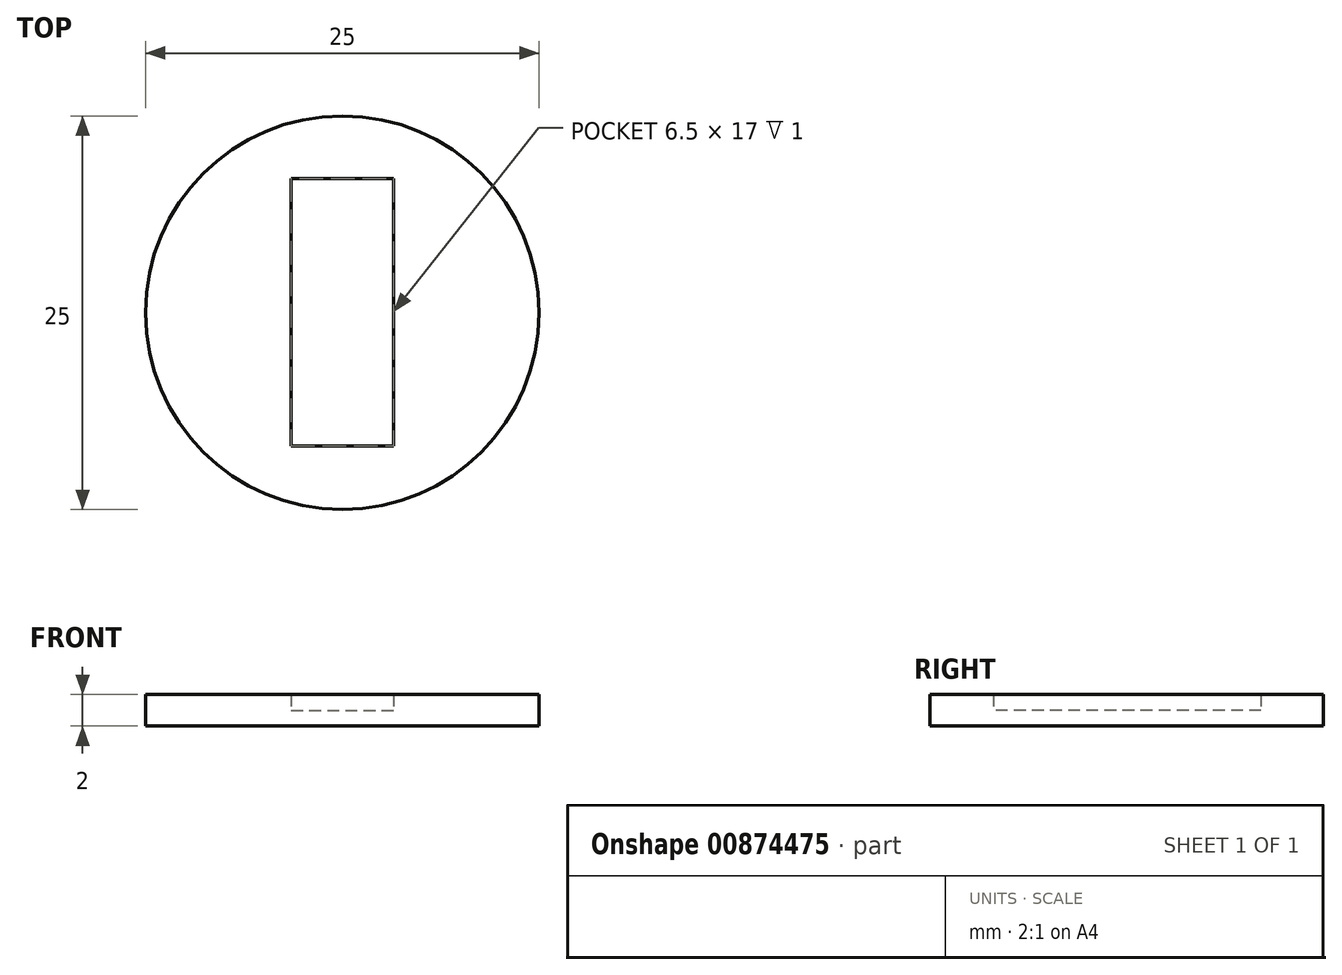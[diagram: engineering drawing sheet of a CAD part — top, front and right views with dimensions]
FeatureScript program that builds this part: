
annotation { "Feature Type Name" : "Feature", "Feature Type Description" : "" }
export const myFeature = defineFeature(function(context is Context, id is Id, definition is map)
    precondition{}
    {
        {
            var Q0;
            Q0=qCreatedBy(makeId("Top.planeOp"),FACE);
            var sketch = newSketch(context, id + "F0", { "sketchPlane" : qUnion([Q0])});
            skCircle(sketch, "E0", {"center": v(11.25, -11.05) * mm, "radius": 12.5 * mm});
            skLineSegment(sketch, "E1.bottom", {"start": v(8, -2.52) * mm, "end": v(14.5, -2.52) * mm});
            skLineSegment(sketch, "E1.top", {"start": v(8, -19.52) * mm, "end": v(14.5, -19.52) * mm});
            skLineSegment(sketch, "E1.left", {"start": v(8, -2.52) * mm, "end": v(8, -19.52) * mm});
            skLineSegment(sketch, "E1.right", {"start": v(14.5, -2.52) * mm, "end": v(14.5, -19.52) * mm});
            skSolve(sketch);
        }
        {
            var Q0;
            Q0=makeQuery(id+"F0.imprint","IMPRINT",FACE,{"disambiguationData":[TD([[makeQuery(id+"F0.imprint","IMPRINT",EDGE,{"derivedFrom":sQuery(id+"F0.wireOp",EDGE,"E1.bottom")}),-1.0]])]});
            extrude(context, id + "F1", {"entities" : qUnion([Q0]), "depth" : 1 * mm, "offsetDistance" : 25 * mm});
        }
        {
            var Q0;
            Q0 = qSketchRegion(id + "F0", true);
            extrude(context, id + "F2", {"entities" : qUnion([Q0]), "operationType" : NewBodyOperationType.ADD, "depth" : 2 * mm, "offsetDistance" : 25 * mm});
        }
    });
